# Revit family: LAMP_MAUI DECO G2
name_source: partatom
category: Modelos genéricos
revit_build: Autodesk Revit 2018 (Build: 20190510_1515(x64)
units: mm (PartAtom-declared; Revit-internal decimal feet)

## family parameters
Anfitrión = Cara
Compartido = No
Corte con vacíos al cargar = No
Cota de conector redondo = Diámetro de uso
Puede alojar armadura = No
Punto de cálculo de habitación = No
Tipo de pieza = Normal

## types (6) — shared parameters
CRI = 80
Diameter = 130 mm  [stored 0.426509 ft]
Elevación por defecto = 1219 mm
Fabricante = LAMP
Gear = Electronic
Height = 1250 mm  [stored 4.10105 ft]
Initial color = 3000 K
Installation instructions = http://www.lamp.es
Insulation class = II
LED Lifetime = 50.000 L90 B10
Lamp = HIGH POWER LED
Last update = 24/02/2022
Luminaire type = Indoor - Surface downlight
MacAdam = 3
Manufacturer URL = http://www.lamp.es
Manufacturer country = Spain
Manufacturer name = LAMP
Power Supply = 110-277V 50/60Hz
Product URL = http://www.lamp.es
Product datasheet = http://www.lamp.es
Protection rating = IP20
Type = HIGH POWER NICHIA
Weight = 1.80 kg

## per-type parameters (varying)
| type | Descripción | Efficacy | Finish | Initial intensity | Material soporte | Modelo | Photometric web file | Plum | Power | Product code |
| 597LM 3000 BLACK SPOT | MAUI DECO G2 SUS 800 WW SP BK. | 73 lm/W | Texturised graphite | 597 lm | LAMP_Aluminio cuerpo Maui NG | MA2SD08SP830NB | Cabeza Maui deco : 597LM 3000 BLACK SPOT | 8 W | 7 W | MA2SD08SP830NB |
| 597LM 3000 CHROME SPOT | MAUI DECO G2 SUS 800 WW SP CR. | 73 lm/W | Gloss grey + Alodine 1500 | 597 lm | LAMP_Aluminio cuerpo Maui CR | MA2SD08SP830NR | Cabeza Maui deco : 597LM 3000 CHROME SPOT | 8 W | 7 W | MA2SD08SP830NR |
| 597LM 3000 WHITE SPOT | MAUI DECO G2 SUS 800 WW SP WH. | 73 lm/W | 9010 Textured | 597 lm | LAMP_Aluminio cuerpo Maui BL | MA2SD08SP830NW | Cabeza Maui deco : 597LM 3000 WHITE SPOT | 8 W | 7 W | MA2SD08SP830NW |
| 1243LM 3000 BLACK SPOT | MAUI DECO G2 SUS 1500 WW SP BK. | 82 lm/W | Texturised graphite | 1243 lm | LAMP_Aluminio cuerpo Maui NG | MA2SD15SP830NB | Cabeza Maui deco : 1243LM 3000 BLACK SPOT | 15 W | 14 W | MA2SD15SP830NB |
| 1243LM 3000 CHROME SPOT | MAUI DECO G2 SUS 1500 WW SP CR. | 82 lm/W | Gloss grey + Alodine 1500 | 1243 lm | LAMP_Aluminio cuerpo Maui CR | MA2SD15SP830NR | Cabeza Maui deco : 1243LM 3000 CHROME SPOT | 15 W | 14 W | MA2SD15SP830NR |
| 1243LM 3000 WHITE SPOT | MAUI DECO G2 SUS 1500 WW SP WH. | 82 lm/W | 9010 Textured | 1243 lm | LAMP_Aluminio cuerpo Maui BL | MA2SD15SP830NW | Cabeza Maui deco : 1243LM 3000 WHITE SPOT | 15 W | 14 W | MA2SD15SP830NW |

note: [stored X ft] marks values corroborated as IEEE doubles in the binary element streams (Revit-internal decimal feet)
